# Revit family: Vistafold_Sliding_Folding_7_Standard
name_source: partatom
category: Doors
revit_build: Autodesk Revit 2014 (Build: 20130308_1515(x64)
units: mm (PartAtom-declared; Revit-internal decimal feet)

## types (28) — shared parameters
All Available Glazing Numbers = The rows below list the available glazing materials for this window:
Centered In Wall = Yes
DG Air Gap Thickness = 12 mm  [stored 0.0393701 ft]
DG Thickness Calc = 6 mm  [stored 0.019685 ft]
Description = Sliding folding door, 7 panel
Double Glazing Gasket Material = Double Glazing Gasket Material
Frame Thickness = 75 mm  [stored 0.246063 ft]
Limit Door Height Min = 367 mm  [stored 1.20407 ft]
Limit Door Width Min = 2192 mm  [stored 7.1916 ft]
Limit Sash Height Min = 300 mm  [stored 0.984252 ft]
Limit Sash Width Min = 300 mm  [stored 0.984252 ft]
Manufacturer = Crealco
Max System DG One Piece Thickness = 6 mm  [stored 0.019685 ft]
Max System DG Unit Thickness = 25 mm  [stored 0.082021 ft]
Model = Vistafold
Number Of Sash Inserts = 7
Rough Width = 3 mm  [stored 0.00984252 ft]
Sash Bottom Gap = 33 mm  [stored 0.108268 ft]
Sash Frame Seal = 3 mm  [stored 0.00984252 ft]
Sash Side Gap = 34 mm  [stored 0.111549 ft]
Sash Spacing Gap = 4 mm  [stored 0.0131234 ft]
Sash Top Gap = 34 mm  [stored 0.111549 ft]
Thickness = 758 mm
URL = http://www.crealco.co.za
Wall Closure = By host
zero-valued in all types: Custom Frame Offset From Exterior, Default Sill Height, IGDB or SAGDB Number

## per-type parameters (varying)
| type | Custom Door Height | Custom Door Width | Custom Windload | Height | Intruderprufe Insulated LowE SHGC Value | Intruderprufe Insulated LowE U Value | Intruderprufe Insulated SHGC Value | Intruderprufe Insulated U Value | Intruderprufe LowE SHGC Value | Intruderprufe LowE U Value | Intruderprufe SHGC Value | Intruderprufe U Value | Limit Door Height Max | Limit Door Width Max | Limit Sash Height Max | Limit Sash Width Max | Max Pane Area | Sash Height | Sash Width | Toughened Safety SHGC Value | Toughened Safety U Value | Width | Windload Design |
| Vistafold-7-2421-1000Pa | 2090 mm  [stored 6.85696 ft] | 2390 mm  [stored 7.84121 ft] | 1000 mm  [stored 3.28084 ft] | 2090 mm  [stored 6.85696 ft] | 0.631 | 4.4 | 0.399 | 4.72 | 0.401 | 5.26 | 0.46 | 6.3 | 2467 mm  [stored 8.09383 ft] | 6392 mm | 2400 mm | 900 mm  [stored 2.95276 ft] | 0.49 m² | 2023 mm  [stored 6.63714 ft] | 328 mm | 0.486 | 6.39 | 2390 mm  [stored 7.84121 ft] | 1000 mm  [stored 3.28084 ft] |
| Vistafold-7-2421-1500Pa | 2090 mm  [stored 6.85696 ft] | 2390 mm  [stored 7.84121 ft] | 1500 mm  [stored 4.92126 ft] | 2090 mm  [stored 6.85696 ft] | 0.631 | 4.4 | 0.399 | 4.72 | 0.401 | 5.26 | 0.46 | 6.3 | 2167 mm | 4292 mm | 2100 mm | 600 mm  [stored 1.9685 ft] | 0.49 m² | 2023 mm  [stored 6.63714 ft] | 328 mm | 0.486 | 6.39 | 2390 mm  [stored 7.84121 ft] | 1500 mm  [stored 4.92126 ft] |
| Vistafold-7-2721-1000Pa | 2090 mm  [stored 6.85696 ft] | 2590 mm | 1000 mm  [stored 3.28084 ft] | 2090 mm  [stored 6.85696 ft] | 0.384 | 4.17 | 0.424 | 4.54 | 0.428 | 5.13 | 0.49 | 6.26 | 2467 mm  [stored 8.09383 ft] | 6392 mm | 2400 mm | 900 mm  [stored 2.95276 ft] | 0.54 m² | 2023 mm  [stored 6.63714 ft] | 357 mm | 0.518 | 6.35 | 2590 mm | 1000 mm  [stored 3.28084 ft] |
| Vistafold-7-2721-1500Pa | 2090 mm  [stored 6.85696 ft] | 2590 mm | 1500 mm  [stored 4.92126 ft] | 2090 mm  [stored 6.85696 ft] | 0.384 | 4.17 | 0.424 | 4.54 | 0.428 | 5.13 | 0.49 | 6.26 | 2167 mm | 4292 mm | 2100 mm | 600 mm  [stored 1.9685 ft] | 0.54 m² | 2023 mm  [stored 6.63714 ft] | 357 mm | 0.518 | 6.35 | 2590 mm | 1500 mm  [stored 4.92126 ft] |
| Vistafold-7-3021-1000Pa | 2090 mm  [stored 6.85696 ft] | 2990 mm | 1000 mm  [stored 3.28084 ft] | 2090 mm  [stored 6.85696 ft] | 0.403 | 4 | 0.445 | 4.4 | 0.449 | 5.03 | 0.514 | 6.22 | 2467 mm  [stored 8.09383 ft] | 6392 mm | 2400 mm | 900 mm  [stored 2.95276 ft] | 0.65 m² | 2023 mm  [stored 6.63714 ft] | 414 mm  [stored 1.35827 ft] | 0.544 | 6.32 | 2990 mm | 1000 mm  [stored 3.28084 ft] |
| Vistafold-7-3021-1500Pa | 2090 mm  [stored 6.85696 ft] | 2990 mm | 1500 mm  [stored 4.92126 ft] | 2090 mm  [stored 6.85696 ft] | 0.403 | 4 | 0.445 | 4.4 | 0.449 | 5.03 | 0.514 | 6.22 | 2167 mm | 4292 mm | 2100 mm | 600 mm  [stored 1.9685 ft] | 0.65 m² | 2023 mm  [stored 6.63714 ft] | 414 mm  [stored 1.35827 ft] | 0.544 | 6.32 | 2990 mm | 1500 mm  [stored 4.92126 ft] |
| Vistafold-7-3321-1000Pa | 2090 mm  [stored 6.85696 ft] | 3290 mm | 1000 mm  [stored 3.28084 ft] | 2090 mm  [stored 6.85696 ft] | 0.418 | 3.85 | 0.462 | 4.28 | 0.467 | 4.94 | 0.533 | 6.19 | 2467 mm  [stored 8.09383 ft] | 6392 mm | 2400 mm | 900 mm  [stored 2.95276 ft] | 0.74 m² | 2023 mm  [stored 6.63714 ft] | 457 mm | 0.565 | 6.29 | 3290 mm | 1000 mm  [stored 3.28084 ft] |
| Vistafold-7-3321-1500Pa | 2090 mm  [stored 6.85696 ft] | 3290 mm | 1500 mm  [stored 4.92126 ft] | 2090 mm  [stored 6.85696 ft] | 0.418 | 3.85 | 0.462 | 4.28 | 0.467 | 4.94 | 0.533 | 6.19 | 2167 mm | 4292 mm | 2100 mm | 600 mm  [stored 1.9685 ft] | 0.74 m² | 2023 mm  [stored 6.63714 ft] | 457 mm | 0.565 | 6.29 | 3290 mm | 1500 mm  [stored 4.92126 ft] |
| Vistafold-7-3621-1000Pa | 2090 mm  [stored 6.85696 ft] | 3590 mm | 1000 mm  [stored 3.28084 ft] | 2090 mm  [stored 6.85696 ft] | 0.43 | 3.7 | 0.476 | 4.15 | 0.481 | 5.25 | 0.553 | 6.16 | 2467 mm  [stored 8.09383 ft] | 6392 mm | 2400 mm | 900 mm  [stored 2.95276 ft] | 0.82 m² | 2023 mm  [stored 6.63714 ft] | 500 mm  [stored 1.64042 ft] | 0.585 | 6.27 | 3590 mm | 1000 mm  [stored 3.28084 ft] |
| Vistafold-7-3621-1500Pa | 2090 mm  [stored 6.85696 ft] | 3590 mm | 1500 mm  [stored 4.92126 ft] | 2090 mm  [stored 6.85696 ft] | 0.43 | 3.7 | 0.476 | 4.15 | 0.481 | 5.25 | 0.553 | 6.16 | 2167 mm | 4292 mm | 2100 mm | 600 mm  [stored 1.9685 ft] | 0.82 m² | 2023 mm  [stored 6.63714 ft] | 500 mm  [stored 1.64042 ft] | 0.585 | 6.27 | 3590 mm | 1500 mm  [stored 4.92126 ft] |
| Vistafold-7-3921-1000Pa | 2090 mm  [stored 6.85696 ft] | 3890 mm | 1000 mm  [stored 3.28084 ft] | 2090 mm  [stored 6.85696 ft] | 0.441 | 3.6 | 0.488 | 4.07 | 0.493 | 5.16 | 0.566 | 6.14 | 2467 mm  [stored 8.09383 ft] | 6392 mm | 2400 mm | 900 mm  [stored 2.95276 ft] | 0.91 m² | 2023 mm  [stored 6.63714 ft] | 543 mm | 0.6 | 6.25 | 3890 mm | 1000 mm  [stored 3.28084 ft] |
| Vistafold-7-3921-1500Pa | 2090 mm  [stored 6.85696 ft] | 3890 mm | 1500 mm  [stored 4.92126 ft] | 2090 mm  [stored 6.85696 ft] | 0.441 | 3.6 | 0.488 | 4.07 | 0.493 | 5.16 | 0.566 | 6.14 | 2167 mm | 4292 mm | 2100 mm | 600 mm  [stored 1.9685 ft] | 0.91 m² | 2023 mm  [stored 6.63714 ft] | 543 mm | 0.6 | 6.25 | 3890 mm | 1500 mm  [stored 4.92126 ft] |
| Vistafold-7-4221-1000Pa | 2090 mm  [stored 6.85696 ft] | 4190 mm | 1000 mm  [stored 3.28084 ft] | 2090 mm  [stored 6.85696 ft] | 0.45 | 3.52 | 0.498 | 4 | 0.504 | 5.08 | 0.578 | 6.12 | 2467 mm  [stored 8.09383 ft] | 6392 mm | 2400 mm | 900 mm  [stored 2.95276 ft] | 0.99 m² | 2023 mm  [stored 6.63714 ft] | 585 mm | 0.612 | 6.23 | 4190 mm | 1000 mm  [stored 3.28084 ft] |
| Vistafold-7-4221-1500Pa | 2090 mm  [stored 6.85696 ft] | 4190 mm | 1500 mm  [stored 4.92126 ft] | 2090 mm  [stored 6.85696 ft] | 0.45 | 3.52 | 0.498 | 4 | 0.504 | 5.08 | 0.578 | 6.12 | 2167 mm | 4292 mm | 2100 mm | 600 mm  [stored 1.9685 ft] | 0.99 m² | 2023 mm  [stored 6.63714 ft] | 585 mm | 0.612 | 6.23 | 4190 mm | 1500 mm  [stored 4.92126 ft] |
| Vistafold-7-4521-1000Pa | 2090 mm  [stored 6.85696 ft] | 4490 mm | 1000 mm  [stored 3.28084 ft] | 2090 mm  [stored 6.85696 ft] | 0.458 | 3.45 | 0.507 | 3.94 | 0.513 | 5.02 | 0.588 | 6.11 | 2467 mm  [stored 8.09383 ft] | 6392 mm | 2400 mm | 900 mm  [stored 2.95276 ft] | 1.07 m² | 2023 mm  [stored 6.63714 ft] | 628 mm | 0.623 | 6.21 | 4490 mm | 1000 mm  [stored 3.28084 ft] |
| Vistafold-7-4821-1000Pa | 2090 mm  [stored 6.85696 ft] | 4790 mm | 1000 mm  [stored 3.28084 ft] | 2090 mm  [stored 6.85696 ft] | 0.465 | 3.38 | 0.515 | 3.89 | 0.521 | 4.96 | 0.567 | 6.09 | 2467 mm  [stored 8.09383 ft] | 6392 mm | 2400 mm | 900 mm  [stored 2.95276 ft] | 1.16 m² | 2023 mm  [stored 6.63714 ft] | 671 mm | 0.632 | 6.2 | 4790 mm | 1000 mm  [stored 3.28084 ft] |
| Vistafold-7-5121-1000Pa | 2090 mm  [stored 6.85696 ft] | 5090 mm | 1000 mm  [stored 3.28084 ft] | 2090 mm  [stored 6.85696 ft] | 0.471 | 3.32 | 0.521 | 3.85 | 0.528 | 4.91 | 0.605 | 6.08 | 2467 mm  [stored 8.09383 ft] | 6392 mm | 2400 mm | 900 mm  [stored 2.95276 ft] | 1.24 m² | 2023 mm  [stored 6.63714 ft] | 714 mm | 0.641 | 6.19 | 5090 mm | 1000 mm  [stored 3.28084 ft] |
| Vistafold-7-5421-1000Pa | 2090 mm  [stored 6.85696 ft] | 5390 mm | 1000 mm  [stored 3.28084 ft] | 2090 mm  [stored 6.85696 ft] | 0.476 | 3.27 | 0.527 | 3.81 | 0.534 | 4.87 | 0.612 | 6.07 | 2467 mm  [stored 8.09383 ft] | 6392 mm | 2400 mm | 900 mm  [stored 2.95276 ft] | 1.32 m² | 2023 mm  [stored 6.63714 ft] | 757 mm | 0.648 | 6.18 | 5390 mm | 1000 mm  [stored 3.28084 ft] |
| Vistafold-7-5721-1000Pa | 2090 mm  [stored 6.85696 ft] | 5690 mm | 1000 mm  [stored 3.28084 ft] | 2090 mm  [stored 6.85696 ft] | 0.481 | 3.23 | 0.533 | 3.77 | 0.54 | 4.83 | 0.618 | 6.06 | 2467 mm  [stored 8.09383 ft] | 6392 mm | 2400 mm | 900 mm  [stored 2.95276 ft] | 1.41 m² | 2023 mm  [stored 6.63714 ft] | 800 mm | 0.655 | 6.17 | 5690 mm | 1000 mm  [stored 3.28084 ft] |
| Vistafold-7-6021-1000Pa | 2090 mm  [stored 6.85696 ft] | 5990 mm | 1000 mm  [stored 3.28084 ft] | 2090 mm  [stored 6.85696 ft] | 0.485 | 3.19 | 0.538 | 3.74 | 0.545 | 4.79 | 0.623 | 6.05 | 2467 mm  [stored 8.09383 ft] | 6392 mm | 2400 mm | 900 mm  [stored 2.95276 ft] | 1.49 m² | 2023 mm  [stored 6.63714 ft] | 843 mm  [stored 2.76575 ft] | 0.661 | 6.16 | 5990 mm | 1000 mm  [stored 3.28084 ft] |
| Vistafold-7-6321-1000Pa | 2090 mm  [stored 6.85696 ft] | 6290 mm | 1000 mm  [stored 3.28084 ft] | 2090 mm  [stored 6.85696 ft] | 0.489 | 3.15 | 0.542 | 3.71 | 0.55 | 4.76 | 0.628 | 6.04 | 2467 mm  [stored 8.09383 ft] | 6392 mm | 2400 mm | 900 mm  [stored 2.95276 ft] | 1.57 m² | 2023 mm  [stored 6.63714 ft] | 885 mm | 0.666 | 6.15 | 6290 mm | 1000 mm  [stored 3.28084 ft] |
| Vistafold-7-2424-1000Pa | 2390 mm  [stored 7.84121 ft] | 2390 mm  [stored 7.84121 ft] | 1000 mm  [stored 3.28084 ft] | 2390 mm  [stored 7.84121 ft] | 0.365 | 4.36 | 0.403 | 4.69 | 0.405 | 5.23 | 0.465 | 6.29 | 2467 mm  [stored 8.09383 ft] | 4292 mm | 2400 mm | 600 mm  [stored 1.9685 ft] | 0.56 m² | 2323 mm | 328 mm | 0.492 | 6.39 | 2390 mm  [stored 7.84121 ft] | 1000 mm  [stored 3.28084 ft] |
| Vistafold-7-2724-1000Pa | 2390 mm  [stored 7.84121 ft] | 2690 mm | 1000 mm  [stored 3.28084 ft] | 2390 mm  [stored 7.84121 ft] | 0.389 | 4.14 | 0.429 | 4.51 | 0.433 | 5.1 | 0.496 | 6.25 | 2467 mm  [stored 8.09383 ft] | 4292 mm | 2400 mm | 600 mm  [stored 1.9685 ft] | 0.66 m² | 2323 mm | 371 mm | 0.524 | 6.34 | 2690 mm | 1000 mm  [stored 3.28084 ft] |
| Vistafold-7-3024-1000Pa | 2390 mm  [stored 7.84121 ft] | 2990 mm | 1000 mm  [stored 3.28084 ft] | 2390 mm  [stored 7.84121 ft] | 0.407 | 3.96 | 0.45 | 4.36 | 0.454 | 4.99 | 0.52 | 6.21 | 2467 mm  [stored 8.09383 ft] | 4292 mm | 2400 mm | 600 mm  [stored 1.9685 ft] | 0.76 m² | 2323 mm | 414 mm  [stored 1.35827 ft] | 0.55 | 6.31 | 2990 mm | 1000 mm  [stored 3.28084 ft] |
| Vistafold-7-3324-1000Pa | 2390 mm  [stored 7.84121 ft] | 3290 mm | 1000 mm  [stored 3.28084 ft] | 2390 mm  [stored 7.84121 ft] | 0.423 | 3.78 | 0.468 | 4.21 | 0.472 | 5.32 | 0.543 | 6.18 | 2467 mm  [stored 8.09383 ft] | 4292 mm | 2400 mm | 600 mm  [stored 1.9685 ft] | 0.85 m² | 2323 mm | 457 mm | 0.575 | 6.28 | 3290 mm | 1000 mm  [stored 3.28084 ft] |
| Vistafold-7-3624-1000Pa | 2390 mm  [stored 7.84121 ft] | 3590 mm | 1000 mm  [stored 3.28084 ft] | 2390 mm  [stored 7.84121 ft] | 0.435 | 3.66 | 0.482 | 4.11 | 0.487 | 5.22 | 0.559 | 6.15 | 2467 mm  [stored 8.09383 ft] | 4292 mm | 2400 mm | 600 mm  [stored 1.9685 ft] | 0.95 m² | 2323 mm | 500 mm  [stored 1.64042 ft] | 0.592 | 6.25 | 3590 mm | 1000 mm  [stored 3.28084 ft] |
| Vistafold-7-3924-1000Pa | 2390 mm  [stored 7.84121 ft] | 3890 mm | 1000 mm  [stored 3.28084 ft] | 2390 mm  [stored 7.84121 ft] | 0.446 | 3.56 | 0.494 | 4.03 | 0.499 | 5.12 | 0.573 | 6.13 | 2467 mm  [stored 8.09383 ft] | 4292 mm | 2400 mm | 600 mm  [stored 1.9685 ft] | 1.04 m² | 2323 mm | 543 mm | 0.607 | 6.23 | 3890 mm | 1000 mm  [stored 3.28084 ft] |
| Vistafold-7-4224-1000Pa | 2390 mm  [stored 7.84121 ft] | 4190 mm | 1000 mm  [stored 3.28084 ft] | 2390 mm  [stored 7.84121 ft] | 0.455 | 3.47 | 0.504 | 3.96 | 0.51 | 5.05 | 0.585 | 6.11 | 2467 mm  [stored 8.09383 ft] | 4292 mm | 2400 mm | 600 mm  [stored 1.9685 ft] | 1.14 m² | 2323 mm | 585 mm | 0.62 | 6.22 | 4190 mm | 1000 mm  [stored 3.28084 ft] |

note: [stored X ft] marks values corroborated as IEEE doubles in the binary element streams (Revit-internal decimal feet)

## geometry (parser evidence)
native form markers: Sweep x33
no freeform markers — native parametric forms only
